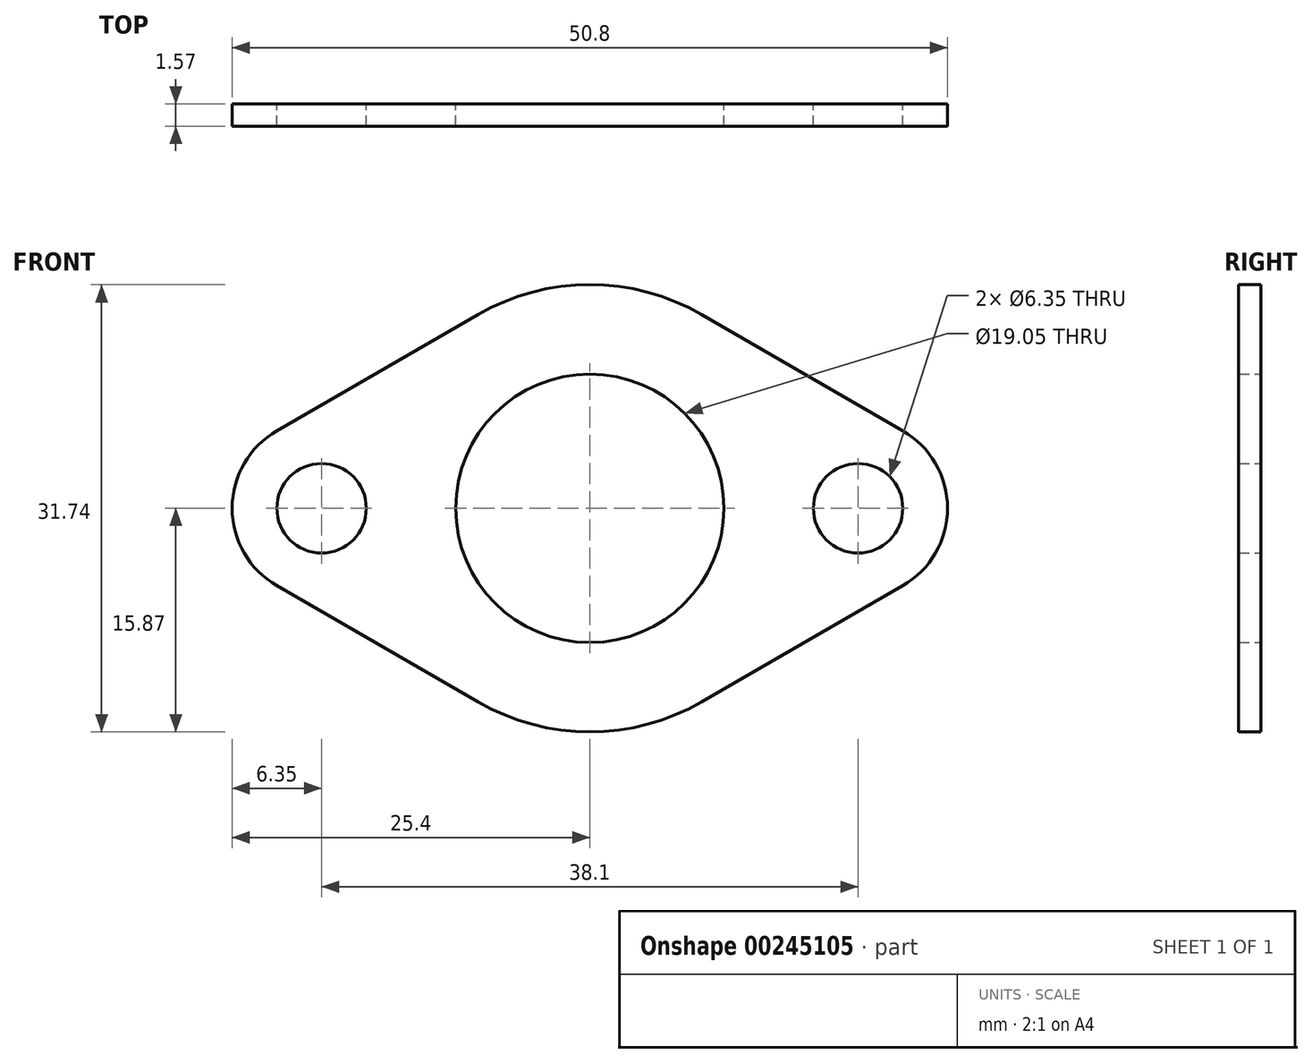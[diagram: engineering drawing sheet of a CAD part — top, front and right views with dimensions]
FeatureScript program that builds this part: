
annotation { "Feature Type Name" : "Feature", "Feature Type Description" : "" }
export const myFeature = defineFeature(function(context is Context, id is Id, definition is map)
    precondition{}
    {
        {
            var Q0;
            Q0=qCreatedBy(makeId("Front.planeOp"),FACE);
            var sketch = newSketch(context, id + "F0", { "sketchPlane" : qUnion([Q0])});
            skCircle(sketch, "E0", {"center": v(-19.05, 0) * mm, "radius": 3.18 * mm});
            skCircle(sketch, "E1", {"center": v(0, 0) * mm, "radius": 9.53 * mm});
            skCircle(sketch, "E2", {"center": v(19.05, 0) * mm, "radius": 3.18 * mm});
            skArc(sketch, "E3", {"start": v(-22.23, 5.5) * mm, "mid": v(-25.4, 0) * mm, "end": v(-22.23, -5.5) * mm});
            skArc(sketch, "E4", {"start": v(22.23, -5.5) * mm, "mid": v(25.4, 0) * mm, "end": v(22.23, 5.5) * mm});
            skLineSegment(sketch, "E5", {"start": v(-22.23, 5.5) * mm, "end": v(-7.94, 13.75) * mm});
            skLineSegment(sketch, "E6", {"start": v(22.23, 5.5) * mm, "end": v(7.94, 13.75) * mm});
            skLineSegment(sketch, "E7", {"start": v(-22.23, -5.5) * mm, "end": v(-7.94, -13.75) * mm});
            skLineSegment(sketch, "E8", {"start": v(22.23, -5.5) * mm, "end": v(7.94, -13.75) * mm});
            skArc(sketch, "E9.trimOffspring", {"start": v(7.94, 13.75) * mm, "mid": v(0, 15.88) * mm, "end": v(-7.94, 13.75) * mm});
            skArc(sketch, "E10.trimOffspring", {"start": v(-7.94, -13.75) * mm, "mid": v(0, -15.88) * mm, "end": v(7.94, -13.75) * mm});
            skLineSegment(sketch, "E11", {"start": v(-22.23, 0) * mm, "end": v(-15.88, 0) * mm});
            skLineSegment(sketch, "E12", {"start": v(-9.53, 0) * mm, "end": v(9.53, 0) * mm});
            skLineSegment(sketch, "E13", {"start": v(0, 9.53) * mm, "end": v(0, -9.53) * mm});
            skLineSegment(sketch, "E14", {"start": v(15.87, 0) * mm, "end": v(22.22, 0) * mm});
            skLineSegment(sketch, "E15", {"start": v(19.05, 3.17) * mm, "end": v(19.05, -3.18) * mm});
            skLineSegment(sketch, "E16", {"start": v(-19.05, -3.18) * mm, "end": v(-19.05, 3.18) * mm});
            skSolve(sketch);
        }
        {
            var Q0;
            Q0=makeQuery(id+"F0.imprint","IMPRINT",FACE,{"disambiguationData":[TD([[makeQuery(id+"F0.imprint","IMPRINT",EDGE,{"derivedFrom":sQuery(id+"F0.wireOp",EDGE,"E0")}),-1.0]])]});
            extrude(context, id + "F1", {"entities" : qUnion([Q0]), "depth" : 1.57 * mm});
        }
    });
